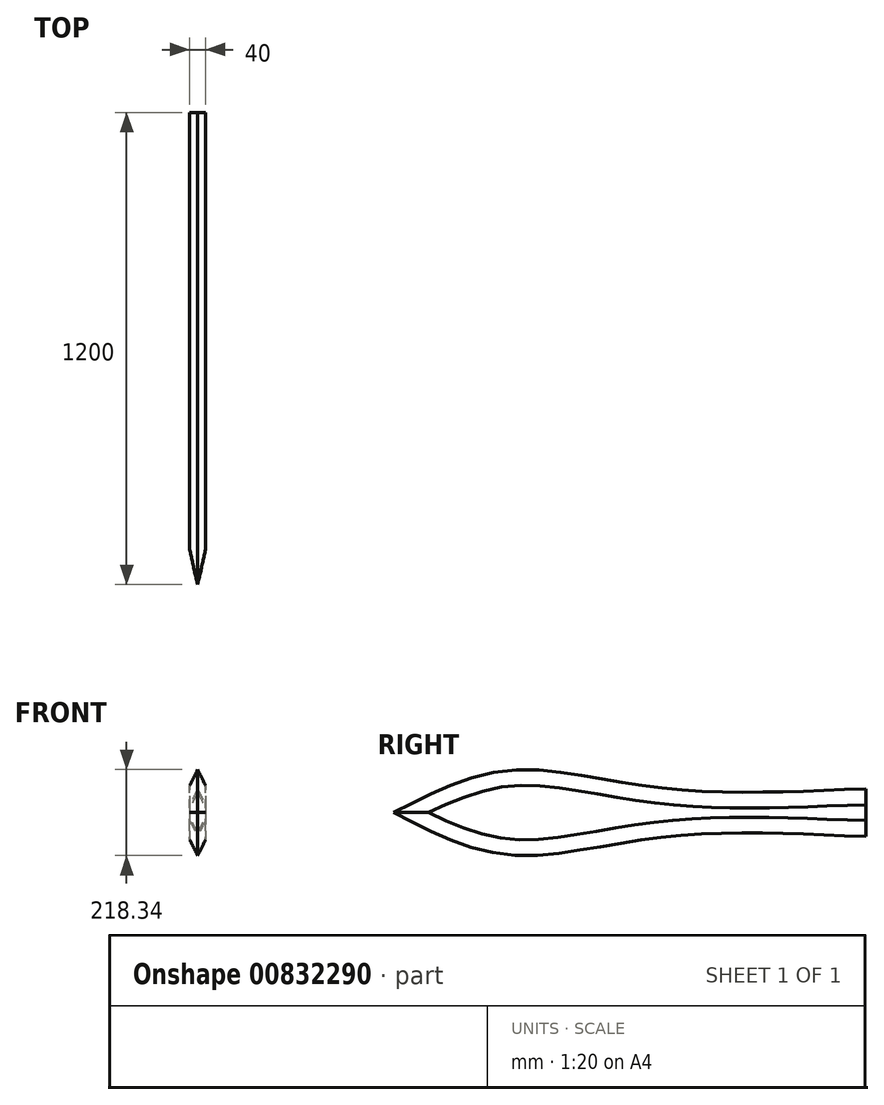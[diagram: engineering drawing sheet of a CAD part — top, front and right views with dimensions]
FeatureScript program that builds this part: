
annotation { "Feature Type Name" : "Feature", "Feature Type Description" : "" }
export const myFeature = defineFeature(function(context is Context, id is Id, definition is map)
    precondition{}
    {
        {
            var Q0;
            Q0=qCreatedBy(makeId("Right.planeOp"),FACE);
            var sketch = newSketch(context, id + "F0", { "sketchPlane" : qUnion([Q0])});
            skFitSpline(sketch, "E0", {"points": [v(0, 60) * mm, v(-471.93, 58.18) * mm, v(-896.1, 108.24) * mm, v(-1200, 0) * mm], "startDerivative": vector(-583.4, 0) * mm, "endDerivative": vector(-1094.13, -562.87) * mm});
            skFitSpline(sketch, "E1.MirrorCS", {"points": [v(0, -60) * mm, v(-471.93, -58.18) * mm, v(-896.1, -108.24) * mm, v(-1200, 0) * mm], "startDerivative": vector(-583.4, 0) * mm, "endDerivative": vector(-1094.13, 562.87) * mm});
            skLineSegment(sketch, "E2", {"start": v(0, 60) * mm, "end": v(0, -60) * mm});
            skSolve(sketch);
        }
        {
            var Q0;
            Q0=makeQuery(id+"F0.imprint","IMPRINT",FACE,{"disambiguationData":[TD([[makeQuery(id+"F0.imprint","IMPRINT",EDGE,{"derivedFrom":sQuery(id+"F0.wireOp",EDGE,"E0")}),1.0]])]});
            extrude(context, id + "F1", {"entities" : qUnion([Q0]), "depth" : 20 * mm, "offsetDistance" : 25 * mm});
        }
        {
            var Q0;
            Q0=makeQuery(id+"F1.opExtrude","CAP_EDGE",EDGE,{"disambiguationData":[OSD([sQuery(id+"F0.wireOp",EDGE,"E0")])],"isStart":false});
            var Q1;
            Q1=makeQuery(id+"F1.opExtrude","CAP_EDGE",EDGE,{"disambiguationData":[OSD([sQuery(id+"F0.wireOp",EDGE,"E1.MirrorCS")])],"isStart":false});
            chamfer(context, id + "F2", {"entities" : qUnion([Q0, Q1]), "chamferType" : ChamferType.TWO_OFFSETS, "width1" : 40 * mm, "oppositeDirection" : false, "width2" : 20 * mm, "tangentPropagation" : true});
        }
        {
            var Q0;
            Q0=makeQuery(id+"F1.opExtrude","SWEPT_BODY",BODY,{"disambiguationData":[OSD([sQuery(id+"F0.wireOp",EDGE,"E0"),sQuery(id+"F0.wireOp",EDGE,"E1.MirrorCS"),sQuery(id+"F0.wireOp",EDGE,"E2")])]});
            var Q1;
            Q1=makeQuery(id+"F1.opExtrude","CAP_FACE",FACE,{"disambiguationData":[OSD([sQuery(id+"F0.wireOp",EDGE,"E0"),sQuery(id+"F0.wireOp",EDGE,"E1.MirrorCS"),sQuery(id+"F0.wireOp",EDGE,"E2")])],"isStart":true});
            mirror(context, id + "F3", {"operationType" : NewBodyOperationType.ADD, "entities" : qUnion([Q0]), "mirrorPlane" : qUnion([Q1])});
        }
    });
